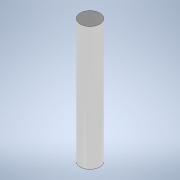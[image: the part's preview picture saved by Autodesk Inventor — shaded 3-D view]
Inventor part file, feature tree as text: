
AUTODESK INVENTOR PART (.ipt)
format: ipt  version: 2022 (Build 260153000, 153)  size: 95,744 bytes
history: native  units: mm
features: extrude x1, sketch x1
ambient origin geometry x8: Origin, YZ Plane, XZ Plane, XY Plane, X Axis, Y Axis, Z Axis, Center Point
bodies: Solid1 (feature_tree)
feature tree (2):
  extrude  "Extrusion1"  Depth=14.0mm TaperAngle=0.0deg
  sketch  "Sketch1"  dims[d0=2.2mm d1=14.0mm d2=0.0mm]
